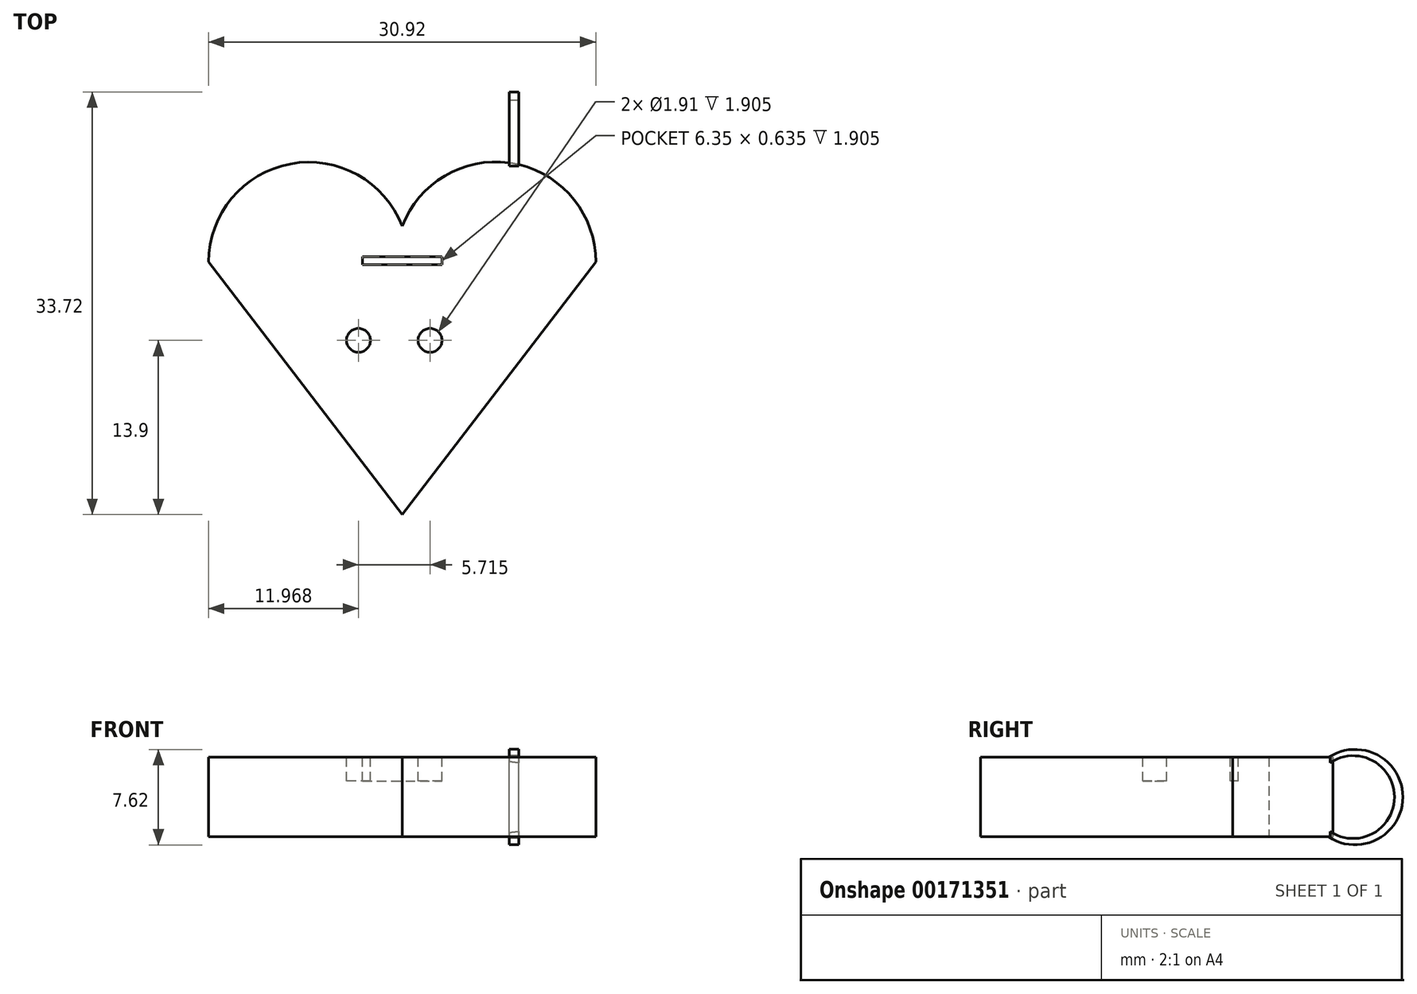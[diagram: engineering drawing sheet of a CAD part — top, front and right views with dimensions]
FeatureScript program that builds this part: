
annotation { "Feature Type Name" : "Feature", "Feature Type Description" : "" }
export const myFeature = defineFeature(function(context is Context, id is Id, definition is map)
    precondition{}
    {
        {
            var Q0;
            Q0=qCreatedBy(makeId("Top.planeOp"),FACE);
            var sketch = newSketch(context, id + "F0", { "sketchPlane" : qUnion([Q0])});
            skLineSegment(sketch, "E0", {"start": v(0, 0) * mm, "end": v(15.46, 20.15) * mm});
            skLineSegment(sketch, "E1", {"start": v(0, 0) * mm, "end": v(-15.46, 20.15) * mm});
            skArc(sketch, "E2", {"start": v(0, 23.02) * mm, "mid": v(-8.92, 27.99) * mm, "end": v(-15.46, 20.15) * mm});
            skPoint(sketch, "E2.startSnap0", {"position": v(0, 20.15) * mm});
            skArc(sketch, "E3", {"start": v(15.46, 20.15) * mm, "mid": v(8.92, 28) * mm, "end": v(0, 23.02) * mm});
            skSolve(sketch);
        }
        {
            var Q0;
            Q0=makeQuery(id+"F0.imprint","IMPRINT",FACE,{"disambiguationData":[TD([[makeQuery(id+"F0.imprint","IMPRINT",EDGE,{"derivedFrom":sQuery(id+"F0.wireOp",EDGE,"E0")}),1.0]])]});
            extrude(context, id + "F1", {"entities" : qUnion([Q0]), "depth" : 6.35 * mm});
        }
        {
            var Q0;
            Q0=makeQuery(id+"F1.opExtrude","CAP_FACE",FACE,{"disambiguationData":[OSD([sQuery(id+"F0.wireOp",EDGE,"E0"),sQuery(id+"F0.wireOp",EDGE,"E1"),sQuery(id+"F0.wireOp",EDGE,"E2"),sQuery(id+"F0.wireOp",EDGE,"E3")])],"isStart":false});
            var sketch = newSketch(context, id + "F2", { "sketchPlane" : qUnion([Q0])});
            skLineSegment(sketch, "E4.bottom", {"start": v(-3.17, 20.57) * mm, "end": v(3.18, 20.57) * mm});
            skLineSegment(sketch, "E4.top", {"start": v(-3.17, 19.93) * mm, "end": v(3.18, 19.93) * mm});
            skLineSegment(sketch, "E4.left", {"start": v(-3.17, 20.57) * mm, "end": v(-3.17, 19.93) * mm});
            skLineSegment(sketch, "E4.right", {"start": v(3.18, 20.57) * mm, "end": v(3.18, 19.93) * mm});
            skLineSegment(sketch, "E5.bottom", {"start": v(3.18, 19.93) * mm, "end": v(2.54, 19.93) * mm});
            skLineSegment(sketch, "E5.top", {"start": v(3.18, 12.95) * mm, "end": v(2.54, 12.95) * mm});
            skLineSegment(sketch, "E5.left", {"start": v(3.18, 19.93) * mm, "end": v(3.18, 12.95) * mm});
            skLineSegment(sketch, "E5.right", {"start": v(2.54, 19.93) * mm, "end": v(2.54, 12.95) * mm});
            skLineSegment(sketch, "E6.bottom", {"start": v(-3.17, 19.93) * mm, "end": v(-2.54, 19.93) * mm});
            skLineSegment(sketch, "E6.top", {"start": v(-3.17, 12.95) * mm, "end": v(-2.54, 12.95) * mm});
            skLineSegment(sketch, "E6.left", {"start": v(-3.17, 19.93) * mm, "end": v(-3.17, 12.95) * mm});
            skLineSegment(sketch, "E6.right", {"start": v(-2.54, 19.93) * mm, "end": v(-2.54, 12.95) * mm});
            skLineSegment(sketch, "E7", {"start": v(0, 28.78) * mm, "end": v(0, -5.06) * mm, "construction": true});
            skCircle(sketch, "E8", {"center": v(2.22, 13.9) * mm, "radius": 0.95 * mm});
            skCircle(sketch, "E9", {"center": v(-3.5, 13.9) * mm, "radius": 0.95 * mm});
            skSolve(sketch);
        }
        {
            var Q0;
            {var subQ0=sQuery(id+"F2.wireOp",EDGE,"E8");var subQ1=sQuery(id+"F2.wireOp",EDGE,"E5.right");var subQ2=makeQuery(id+"F2.imprint","INTERSECT",VERTEX,{"disambiguationData":[OD(0.0)],"derivedFrom":[subQ1,subQ0]});Q0=makeQuery(id+"F2.imprint","IMPRINT",FACE,{"disambiguationData":[TD([[makeQuery(id+"F2.imprint","IMPRINT",EDGE,{"disambiguationData":[TD([[subQ2,-1.0]])],"derivedFrom":subQ1}),-1.0]])]});}
            var Q1;
            {var subQ0=sQuery(id+"F2.wireOp",EDGE,"E8");var subQ1=sQuery(id+"F2.wireOp",EDGE,"E5.right");var subQ2=makeQuery(id+"F2.imprint","INTERSECT",VERTEX,{"disambiguationData":[OD(0.0)],"derivedFrom":[subQ1,subQ0]});Q1=makeQuery(id+"F2.imprint","IMPRINT",FACE,{"disambiguationData":[TD([[makeQuery(id+"F2.imprint","IMPRINT",EDGE,{"disambiguationData":[TD([[subQ2,-1.0]])],"derivedFrom":subQ1}),1.0]])]});}
            var Q2;
            {var subQ0=sQuery(id+"F2.wireOp",EDGE,"E5.bottom");Q2=makeQuery(id+"F2.imprint","IMPRINT",FACE,{"disambiguationData":[TD([[makeQuery(id+"F2.imprint","IMPRINT",EDGE,{"derivedFrom":subQ0}),1.0]])]});}
            var Q3;
            Q3=makeQuery(id+"F2.imprint","IMPRINT",FACE,{"disambiguationData":[TD([[makeQuery(id+"F2.imprint","IMPRINT",EDGE,{"derivedFrom":sQuery(id+"F2.wireOp",EDGE,"E4.bottom")}),-1.0]])]});
            var Q4;
            {var subQ0=sQuery(id+"F2.wireOp",EDGE,"E6.bottom");Q4=makeQuery(id+"F2.imprint","IMPRINT",FACE,{"disambiguationData":[TD([[makeQuery(id+"F2.imprint","IMPRINT",EDGE,{"derivedFrom":subQ0}),-1.0]])]});}
            var Q5;
            {var subQ0=sQuery(id+"F2.wireOp",EDGE,"E9");var subQ1=sQuery(id+"F2.wireOp",EDGE,"E6.left");var subQ2=makeQuery(id+"F2.imprint","INTERSECT",VERTEX,{"disambiguationData":[OD(0.0)],"derivedFrom":[subQ1,subQ0]});Q5=makeQuery(id+"F2.imprint","IMPRINT",FACE,{"disambiguationData":[TD([[makeQuery(id+"F2.imprint","IMPRINT",EDGE,{"disambiguationData":[TD([[subQ2,-1.0]])],"derivedFrom":subQ1}),1.0]])]});}
            var Q6;
            {var subQ0=sQuery(id+"F2.wireOp",EDGE,"E9");var subQ1=sQuery(id+"F2.wireOp",EDGE,"E6.left");var subQ2=makeQuery(id+"F2.imprint","INTERSECT",VERTEX,{"disambiguationData":[OD(0.0)],"derivedFrom":[subQ1,subQ0]});Q6=makeQuery(id+"F2.imprint","IMPRINT",FACE,{"disambiguationData":[TD([[makeQuery(id+"F2.imprint","IMPRINT",EDGE,{"disambiguationData":[TD([[subQ2,-1.0]])],"derivedFrom":subQ1}),-1.0]])]});}
            extrude(context, id + "F3", {"entities" : qUnion([Q0, Q1, Q2, Q3, Q4, Q5, Q6]), "operationType" : NewBodyOperationType.REMOVE, "oppositeDirection" : true, "depth" : 1.9 * mm});
        }
        {
            var Q0;
            Q0=makeQuery(id+"F1.opExtrude","CAP_FACE",FACE,{"disambiguationData":[OSD([sQuery(id+"F0.wireOp",EDGE,"E0"),sQuery(id+"F0.wireOp",EDGE,"E1"),sQuery(id+"F0.wireOp",EDGE,"E2"),sQuery(id+"F0.wireOp",EDGE,"E3")])],"isStart":false});
            var sketch = newSketch(context, id + "F4", { "sketchPlane" : qUnion([Q0])});
            skLineSegment(sketch, "E10", {"start": v(8.92, 28) * mm, "end": v(8.92, 0) * mm, "construction": true});
            skLineSegment(sketch, "E11", {"start": v(8.92, 28) * mm, "end": v(0, 28) * mm, "construction": true});
            skSolve(sketch);
        }
        {
            var Q0;
            Q0=qCreatedBy(makeId("Right.planeOp"),FACE);
            cPlane(context, id + "F5", {"entities" : qUnion([Q0]), "cplaneType" : CPlaneType.OFFSET, "offset" : 8.92 * mm, "width" : 152.4 * mm, "height" : 152.4 * mm});
        }
        {
            var Q0;
            Q0=qCreatedBy(id+"F5.planeOp",FACE);
            var sketch = newSketch(context, id + "F6", { "sketchPlane" : qUnion([Q0])});
            skLineSegment(sketch, "E12.0", {"start": v(20.15, 6.35) * mm, "end": v(28.14, 6.35) * mm});
            skLineSegment(sketch, "E12.1", {"start": v(20.15, 0) * mm, "end": v(28.14, 0) * mm});
            skLineSegment(sketch, "E12.2", {"start": v(28, 6.35) * mm, "end": v(0, 6.35) * mm});
            skLineSegment(sketch, "E13", {"start": v(27.8, 6.35) * mm, "end": v(27.8, 0) * mm});
            skArc(sketch, "E14", {"start": v(27.8, 0) * mm, "mid": v(33.72, 3.17) * mm, "end": v(27.8, 6.35) * mm});
            skLineSegment(sketch, "E15", {"start": v(27.8, 6.35) * mm, "end": v(27.8, 5.84) * mm});
            skLineSegment(sketch, "E16", {"start": v(27.8, 0) * mm, "end": v(27.8, 0.5) * mm});
            skArc(sketch, "E17", {"start": v(27.8, 0.5) * mm, "mid": v(33.06, 3.17) * mm, "end": v(27.8, 5.84) * mm});
            skSolve(sketch);
        }
        {
            var Q0;
            Q0=makeQuery(id+"F6.imprint","IMPRINT",FACE,{"disambiguationData":[TD([[makeQuery(id+"F6.imprint","IMPRINT",EDGE,{"derivedFrom":sQuery(id+"F6.wireOp",EDGE,"E14")}),1.0]])]});
            extrude(context, id + "F7", {"entities" : qUnion([Q0]), "operationType" : NewBodyOperationType.ADD, "depth" : 0.38 * mm});
        }
        {
            var Q0;
            Q0=makeQuery(id+"F6.imprint","IMPRINT",FACE,{"disambiguationData":[TD([[makeQuery(id+"F6.imprint","IMPRINT",EDGE,{"derivedFrom":sQuery(id+"F6.wireOp",EDGE,"E14")}),1.0]])]});
            extrude(context, id + "F8", {"entities" : qUnion([Q0]), "operationType" : NewBodyOperationType.ADD, "oppositeDirection" : true, "depth" : 0.38 * mm});
        }
    });
